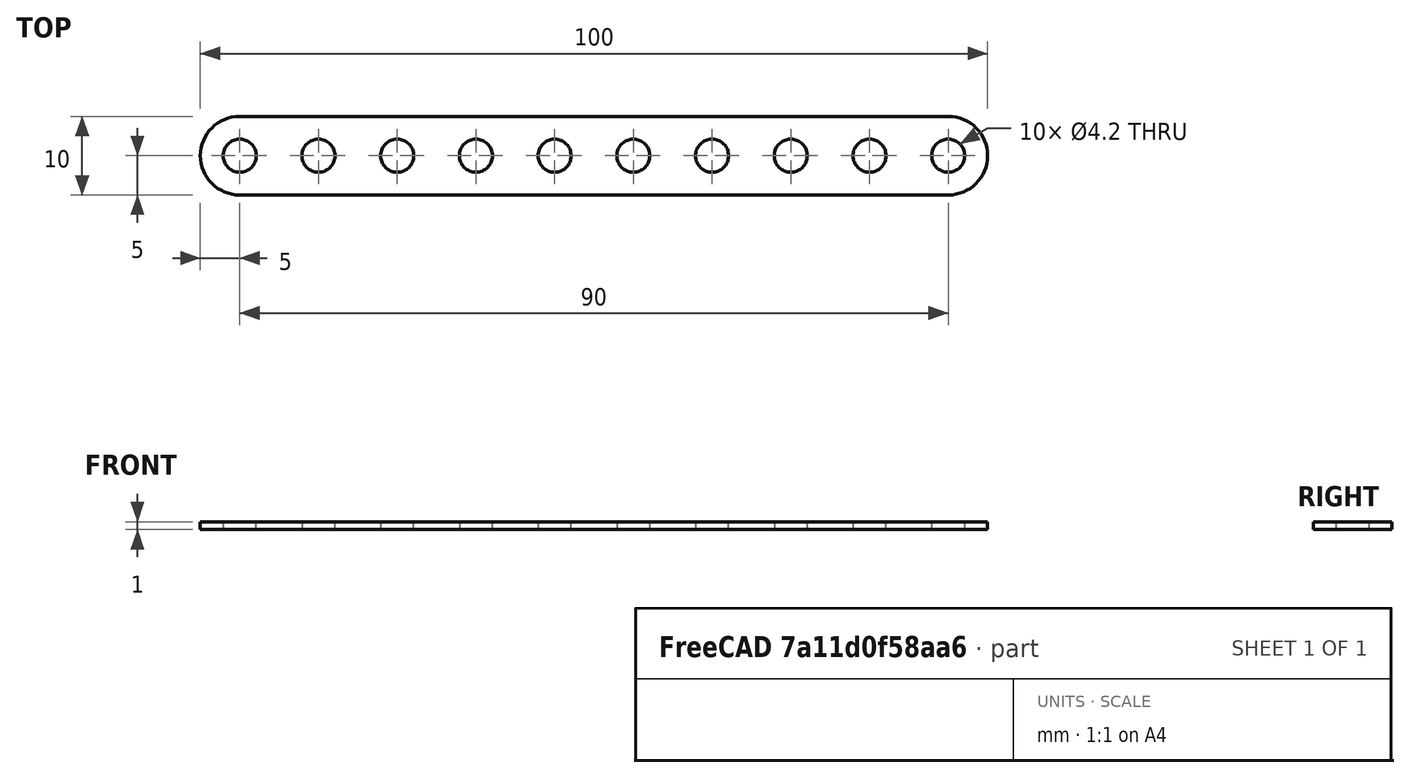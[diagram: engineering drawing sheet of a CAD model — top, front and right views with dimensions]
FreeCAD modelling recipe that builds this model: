
FCSTD DOCUMENT  (FreeCAD 0.16RUnknown)
Label: strip_1x10
License: All rights reserved
LicenseURL: http://en.wikipedia.org/wiki/All_rights_reserved
objects: Sketcher::SketchObject×1, PartDesign::Pad×1
note: 3 computed .brp shape members not serialized (recipe doc carries the construction recipe); baked Part::Feature solids carry a one-line shape summary decoded from their .brp

FEATURE [Sketcher::SketchObject] Sketch
  sketch-geometry (23):
    g0: Circle CenterX=0 CenterY=0 CenterZ=0 NormalX=0 NormalY=0 NormalZ=1 Radius=2.1
    g1: Circle CenterX=10 CenterY=0 CenterZ=0 NormalX=0 NormalY=0 NormalZ=1 Radius=2.1
    g2: LineSegment [constr] StartX=0 StartY=0 StartZ=0 EndX=10 EndY=0 EndZ=0
    g3: Circle CenterX=20 CenterY=0 CenterZ=0 NormalX=0 NormalY=0 NormalZ=1 Radius=2.1
    g4: LineSegment [constr] StartX=10 StartY=0 StartZ=0 EndX=20 EndY=0 EndZ=0
    g5: Circle CenterX=30 CenterY=0 CenterZ=0 NormalX=0 NormalY=0 NormalZ=1 Radius=2.1
    g6: LineSegment [constr] StartX=20 StartY=0 StartZ=0 EndX=30 EndY=0 EndZ=0
    g7: Circle CenterX=40 CenterY=0 CenterZ=0 NormalX=0 NormalY=0 NormalZ=1 Radius=2.1
    g8: LineSegment [constr] StartX=30 StartY=0 StartZ=0 EndX=40 EndY=0 EndZ=0
    g9: ArcOfCircle CenterX=0 CenterY=0 CenterZ=0 NormalX=0 NormalY=0 NormalZ=1 Radius=5 StartAngle=1.5708 EndAngle=4.71239
    g10: ArcOfCircle CenterX=90 CenterY=0 CenterZ=0 NormalX=0 NormalY=0 NormalZ=1 Radius=5 StartAngle=4.71239 EndAngle=7.85398
    g11: LineSegment StartX=1e-12 StartY=-5 StartZ=0 EndX=90 EndY=-5 EndZ=0
    g12: LineSegment StartX=0 StartY=5 StartZ=0 EndX=90 EndY=5 EndZ=0
    g13: Circle CenterX=50 CenterY=0 CenterZ=0 NormalX=0 NormalY=0 NormalZ=1 Radius=2.1
    g14: LineSegment [constr] StartX=40 StartY=0 StartZ=0 EndX=50 EndY=0 EndZ=0
    g15: Circle CenterX=60 CenterY=0 CenterZ=0 NormalX=0 NormalY=0 NormalZ=1 Radius=2.1
    g16: LineSegment [constr] StartX=50 StartY=0 StartZ=0 EndX=60 EndY=0 EndZ=0
    g17: Circle CenterX=70 CenterY=0 CenterZ=0 NormalX=0 NormalY=0 NormalZ=1 Radius=2.1
    g18: LineSegment [constr] StartX=60 StartY=0 StartZ=0 EndX=70 EndY=0 EndZ=0
    g19: Circle CenterX=80 CenterY=0 CenterZ=0 NormalX=0 NormalY=0 NormalZ=1 Radius=2.1
    g20: LineSegment [constr] StartX=70 StartY=0 StartZ=0 EndX=80 EndY=0 EndZ=0
    g21: LineSegment [constr] StartX=80 StartY=0 StartZ=0 EndX=90 EndY=0 EndZ=0
    g22: Circle CenterX=90 CenterY=0 CenterZ=0 NormalX=0 NormalY=0 NormalZ=1 Radius=2.1
  constraints (56):
    c: Radius(g0) = 2.1
    c: Equal(g0,g1) = 5
    c: Coincident(g0,g2)
    c: Coincident(g1,g2)
    c: Equal(g0,g3) = 5
    c: Coincident(g1,g4)
    c: Coincident(g3,g4)
    c: Equal(g2,g4)
    c: Parallel(g4,g2)
    c: Equal(g0,g5) = 5
    c: Coincident(g3,g6)
    c: Coincident(g5,g6)
    c: Equal(g2,g6)
    c: Parallel(g6,g2)
    c: Equal(g0,g7) = 5
    c: Coincident(g5,g8)
    c: Coincident(g7,g8)
    c: Equal(g2,g8)
    c: Parallel(g8,g2)
    c: Coincident(g0,g-1)
    c: Distance(g-1,g1) = 10
    c: Angle(g2,g-1) = 0
    c: Tangent(g9,g12) = 1.5708
    c: Tangent(g9,g11) = -1.5708
    c: Tangent(g11,g10) = -1.5708
    c: Tangent(g12,g10) = 1.5708
    c: Horizontal(g11)
    c: Equal(g9,g10)
    c: Coincident(g-1,g9)
    c: Radius(g9) = 5
    c: Coincident(g7,g14)
    c: Coincident(g13,g14)
    c: Distance(g14) = 10
    c: Angle(g14) = 0
    c: Coincident(g13,g16)
    c: Coincident(g15,g16)
    c: Equal(g14,g16)
    c: Parallel(g16,g14)
    c: Coincident(g15,g18)
    c: Coincident(g17,g18)
    c: Equal(g14,g18)
    c: Parallel(g18,g14)
    c: Coincident(g17,g20)
    c: Coincident(g19,g20)
    c: Equal(g14,g20)
    c: Parallel(g20,g14)
    c: Radius(g19) = 2.1
    c: Equal(g19,g17)
    c: Equal(g19,g15)
    c: Equal(g19,g13)
    c: Coincident(g19,g21)
    c: Distance(g21) = 10
    c: Angle(g21) = 0
    c: Equal(g19,g22) = 2.1
    c: Coincident(g10,g22)
    c: Coincident(g21,g10)
FEATURE [PartDesign::Pad] Pad
  Length = 1
  Length2 = 100
  Sketch = -> Sketch
  Type = 0
